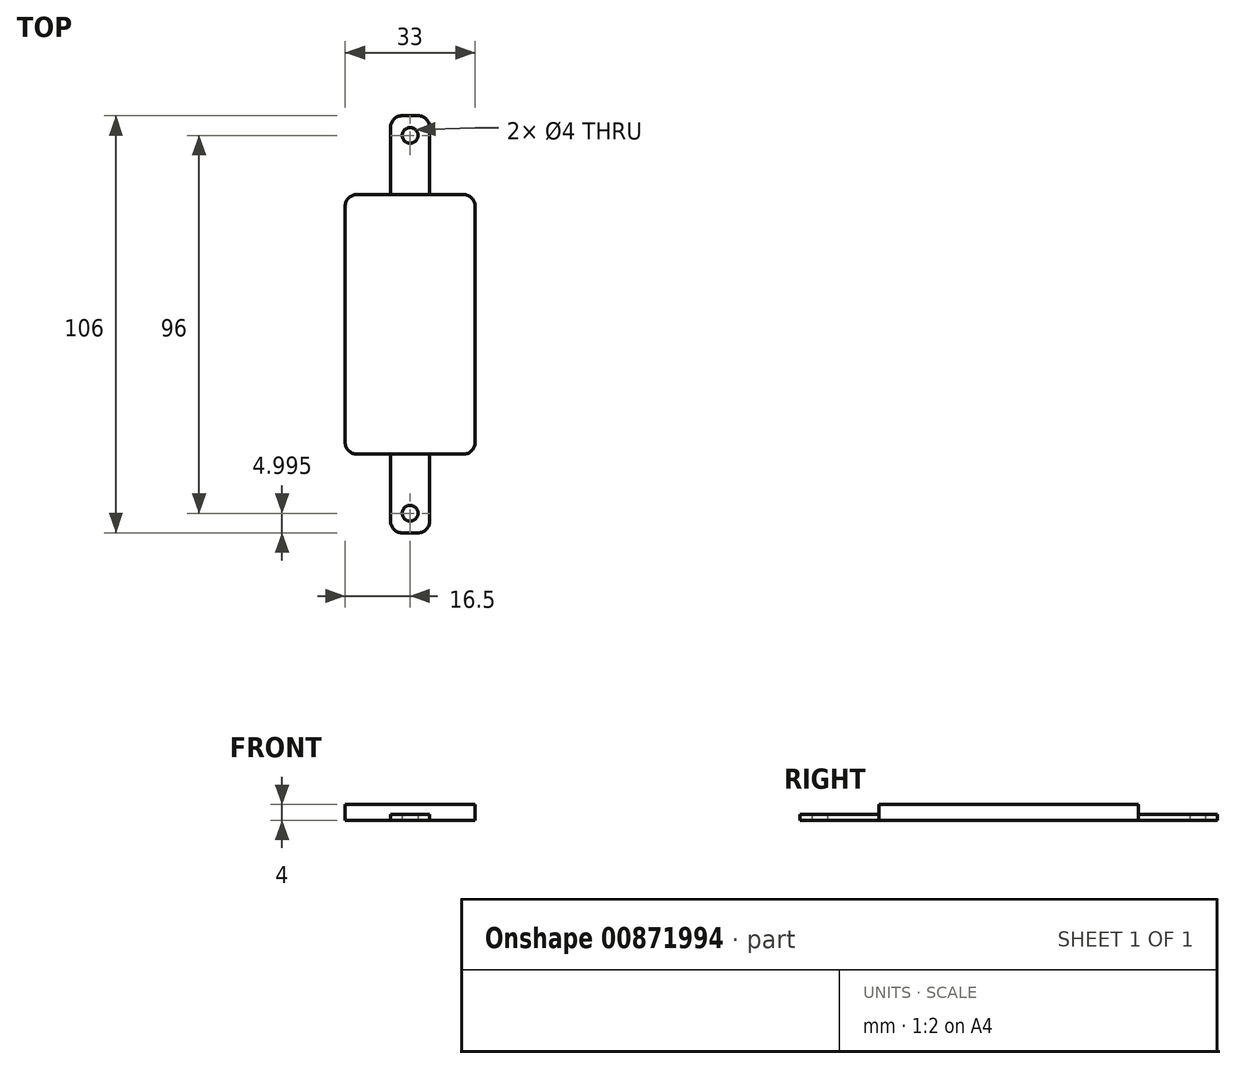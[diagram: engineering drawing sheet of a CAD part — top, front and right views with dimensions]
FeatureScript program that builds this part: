
annotation { "Feature Type Name" : "Feature", "Feature Type Description" : "" }
export const myFeature = defineFeature(function(context is Context, id is Id, definition is map)
    precondition{}
    {
        {
            var Q0;
            Q0=qCreatedBy(makeId("Top.planeOp"),FACE);
            var sketch = newSketch(context, id + "F0", { "sketchPlane" : qUnion([Q0])});
            skLineSegment(sketch, "E0", {"start": v(-16.5, 47.63) * mm, "end": v(-16.5, -18.37) * mm});
            skLineSegment(sketch, "E1", {"start": v(-16.5, -18.37) * mm, "end": v(16.5, -18.37) * mm});
            skLineSegment(sketch, "E2", {"start": v(16.5, -18.37) * mm, "end": v(16.5, 47.63) * mm});
            skLineSegment(sketch, "E3", {"start": v(16.5, 47.63) * mm, "end": v(-16.5, 47.63) * mm});
            skLineSegment(sketch, "E4", {"start": v(-16.5, 47.63) * mm, "end": v(-5, 47.63) * mm});
            skLineSegment(sketch, "E5", {"start": v(-5, 47.63) * mm, "end": v(-5, 67.63) * mm});
            skLineSegment(sketch, "E6", {"start": v(-5, 67.63) * mm, "end": v(5, 67.63) * mm});
            skLineSegment(sketch, "E7", {"start": v(5, 67.63) * mm, "end": v(5, 47.63) * mm});
            skLineSegment(sketch, "E8", {"start": v(5, 47.63) * mm, "end": v(16.5, 47.63) * mm});
            skLineSegment(sketch, "E9", {"start": v(-16.5, -18.37) * mm, "end": v(-5, -18.37) * mm});
            skLineSegment(sketch, "E10", {"start": v(-5, -18.37) * mm, "end": v(-5, -38.37) * mm});
            skLineSegment(sketch, "E11", {"start": v(-5, -38.37) * mm, "end": v(5, -38.37) * mm});
            skLineSegment(sketch, "E12", {"start": v(5, -38.37) * mm, "end": v(5, -18.37) * mm});
            skLineSegment(sketch, "E13", {"start": v(5, -18.37) * mm, "end": v(16.5, -18.37) * mm});
            skCircle(sketch, "E14", {"center": v(0, -33.37) * mm, "radius": 2 * mm});
            skCircle(sketch, "E15", {"center": v(0, 62.63) * mm, "radius": 2 * mm});
            skSolve(sketch);
        }
        {
            var Q0;
            Q0=makeQuery(id+"F0.imprint","IMPRINT",FACE,{"disambiguationData":[TD([[makeQuery(id+"F0.imprint","IMPRINT",EDGE,{"derivedFrom":sQuery(id+"F0.wireOp",EDGE,"E3")}),-1.0]])]});
            var Q1;
            Q1=makeQuery(id+"F0.imprint","IMPRINT",FACE,{"disambiguationData":[TD([[makeQuery(id+"F0.imprint","IMPRINT",EDGE,{"derivedFrom":sQuery(id+"F0.wireOp",EDGE,"E1")}),-1.0]])]});
            extrude(context, id + "F1", {"entities" : qUnion([Q0, Q1]), "depth" : 1.5 * mm, "offsetDistance" : 25 * mm});
        }
        {
            var Q0;
            Q0=makeQuery(id+"F0.imprint","IMPRINT",FACE,{"disambiguationData":[TD([[makeQuery(id+"F0.imprint","IMPRINT",EDGE,{"derivedFrom":sQuery(id+"F0.wireOp",EDGE,"E0")}),1.0]])]});
            extrude(context, id + "F2", {"entities" : qUnion([Q0]), "depth" : 4 * mm, "offsetDistance" : 25 * mm});
        }
        {
            var Q0;
            Q0=makeQuery(id+"F2.opExtrude","SWEPT_EDGE",EDGE,{"disambiguationData":[OSD([sQuery(id+"F0.wireOp",EDGE,"E2"),sQuery(id+"F0.wireOp",EDGE,"E8")])]});
            var Q1;
            Q1=makeQuery(id+"F2.opExtrude","SWEPT_EDGE",EDGE,{"disambiguationData":[OSD([sQuery(id+"F0.wireOp",EDGE,"E0"),sQuery(id+"F0.wireOp",EDGE,"E4")])]});
            var Q2;
            Q2=makeQuery(id+"F2.opExtrude","SWEPT_EDGE",EDGE,{"disambiguationData":[OSD([sQuery(id+"F0.wireOp",EDGE,"E0"),sQuery(id+"F0.wireOp",EDGE,"E9")])]});
            var Q3;
            Q3=makeQuery(id+"F2.opExtrude","SWEPT_EDGE",EDGE,{"disambiguationData":[OSD([sQuery(id+"F0.wireOp",EDGE,"E2"),sQuery(id+"F0.wireOp",EDGE,"E13")])]});
            var Q4;
            Q4=makeQuery(id+"F1.opExtrude","SWEPT_EDGE",EDGE,{"disambiguationData":[OSD([sQuery(id+"F0.wireOp",EDGE,"E10"),sQuery(id+"F0.wireOp",EDGE,"E11")])]});
            var Q5;
            Q5=makeQuery(id+"F1.opExtrude","SWEPT_EDGE",EDGE,{"disambiguationData":[OSD([sQuery(id+"F0.wireOp",EDGE,"E11"),sQuery(id+"F0.wireOp",EDGE,"E12")])]});
            var Q6;
            Q6=makeQuery(id+"F1.opExtrude","SWEPT_EDGE",EDGE,{"disambiguationData":[OSD([sQuery(id+"F0.wireOp",EDGE,"E6"),sQuery(id+"F0.wireOp",EDGE,"E7")])]});
            var Q7;
            Q7=makeQuery(id+"F1.opExtrude","SWEPT_EDGE",EDGE,{"disambiguationData":[OSD([sQuery(id+"F0.wireOp",EDGE,"E5"),sQuery(id+"F0.wireOp",EDGE,"E6")])]});
            fillet(context, id + "F3", {"entities" : qUnion([Q0, Q1, Q2, Q3, Q4, Q5, Q6, Q7]), "radius" : 3 * mm, "tangentPropagation" : true, "allowEdgeOverflow" : false});
        }
    });
